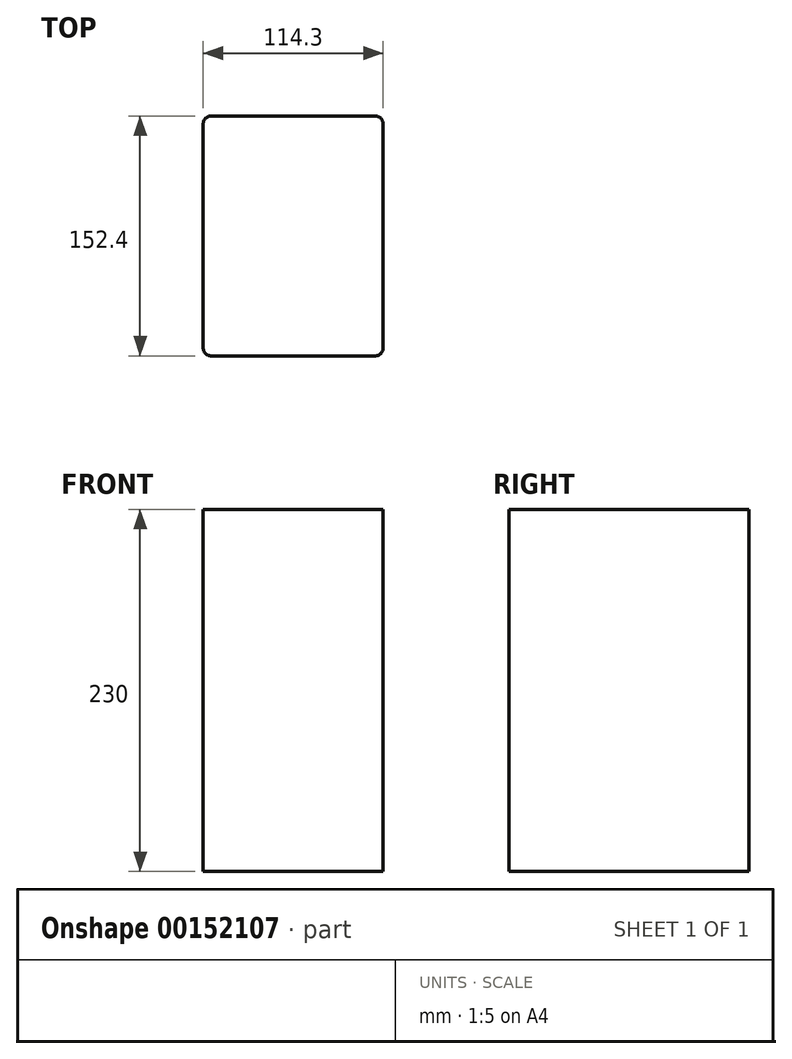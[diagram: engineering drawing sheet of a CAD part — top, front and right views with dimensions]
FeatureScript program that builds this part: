
annotation { "Feature Type Name" : "Feature", "Feature Type Description" : "" }
export const myFeature = defineFeature(function(context is Context, id is Id, definition is map)
    precondition{}
    {
        {
            var Q0;
            Q0=qCreatedBy(makeId("Top.planeOp"),FACE);
            var sketch = newSketch(context, id + "F0", { "sketchPlane" : qUnion([Q0])});
            skLineSegment(sketch, "E0.bottom", {"start": v(0, 0) * mm, "end": v(114.3, 0) * mm});
            skLineSegment(sketch, "E0.top", {"start": v(0, 152.4) * mm, "end": v(114.3, 152.4) * mm});
            skLineSegment(sketch, "E0.left", {"start": v(0, 0) * mm, "end": v(0, 152.4) * mm});
            skLineSegment(sketch, "E0.right", {"start": v(114.3, 0) * mm, "end": v(114.3, 152.4) * mm});
            skSolve(sketch);
        }
        {
            var Q0;
            Q0=makeQuery(id+"F0.imprint","IMPRINT",FACE,{"disambiguationData":[TD([[makeQuery(id+"F0.imprint","IMPRINT",EDGE,{"derivedFrom":sQuery(id+"F0.wireOp",EDGE,"E0.bottom")}),1.0]])]});
            extrude(context, id + "F1", {"entities" : qUnion([Q0]), "depth" : 230 * mm});
        }
        {
            var Q0;
            Q0=makeQuery(id+"F1.opExtrude","SWEPT_EDGE",EDGE,{"disambiguationData":[OSD([sQuery(id+"F0.wireOp",EDGE,"E0.bottom"),sQuery(id+"F0.wireOp",EDGE,"E0.right")])]});
            var Q1;
            Q1=makeQuery(id+"F1.opExtrude","SWEPT_EDGE",EDGE,{"disambiguationData":[OSD([sQuery(id+"F0.wireOp",EDGE,"E0.top"),sQuery(id+"F0.wireOp",EDGE,"E0.right")])]});
            var Q2;
            Q2=makeQuery(id+"F1.opExtrude","SWEPT_EDGE",EDGE,{"disambiguationData":[OSD([sQuery(id+"F0.wireOp",EDGE,"E0.bottom"),sQuery(id+"F0.wireOp",EDGE,"E0.left")])]});
            var Q3;
            Q3=makeQuery(id+"F1.opExtrude","SWEPT_EDGE",EDGE,{"disambiguationData":[OSD([sQuery(id+"F0.wireOp",EDGE,"E0.top"),sQuery(id+"F0.wireOp",EDGE,"E0.left")])]});
            fillet(context, id + "F2", {"entities" : qUnion([Q0, Q1, Q2, Q3]), "radius" : 5.08 * mm, "tangentPropagation" : true, "allowEdgeOverflow" : false});
        }
    });
